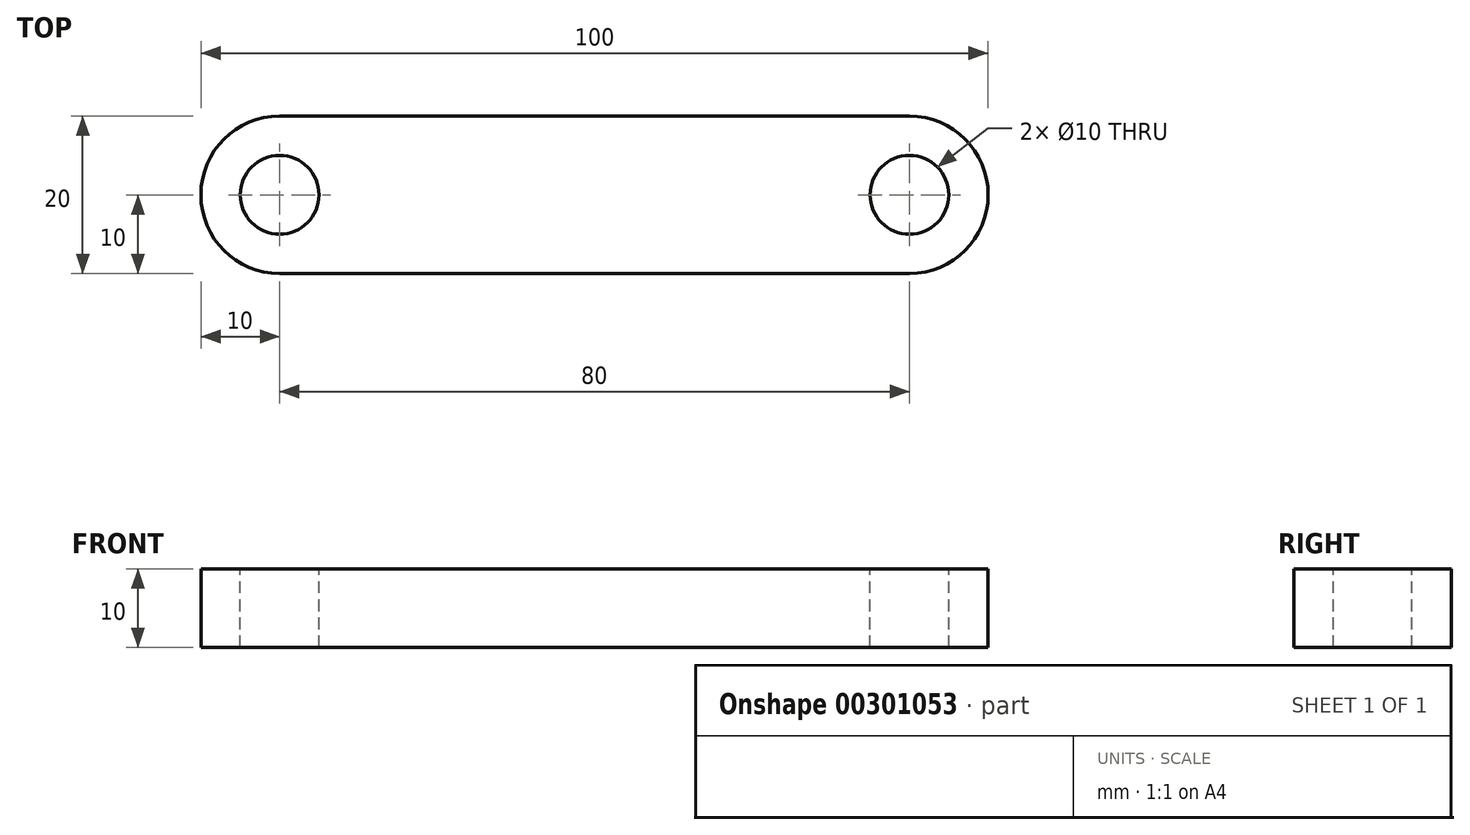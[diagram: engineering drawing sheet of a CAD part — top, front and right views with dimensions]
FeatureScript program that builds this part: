
annotation { "Feature Type Name" : "Feature", "Feature Type Description" : "" }
export const myFeature = defineFeature(function(context is Context, id is Id, definition is map)
    precondition{}
    {
        {
            var Q0;
            Q0=qCreatedBy(makeId("Top.planeOp"),FACE);
            var sketch = newSketch(context, id + "F0", { "sketchPlane" : qUnion([Q0])});
            skLineSegment(sketch, "E0", {"start": v(0, 0) * mm, "end": v(80, 0) * mm});
            skLineSegment(sketch, "E1", {"start": v(0, 20) * mm, "end": v(80, 20) * mm});
            skArc(sketch, "E2", {"start": v(0, 20) * mm, "mid": v(-10, 10) * mm, "end": v(0, 0) * mm});
            skArc(sketch, "E3", {"start": v(80, 0) * mm, "mid": v(90, 10) * mm, "end": v(80, 20) * mm});
            skSolve(sketch);
        }
        {
            var Q0;
            Q0=makeQuery(id+"F0.imprint","IMPRINT",FACE,{"disambiguationData":[TD([[makeQuery(id+"F0.imprint","IMPRINT",EDGE,{"derivedFrom":sQuery(id+"F0.wireOp",EDGE,"E0")}),1.0]])]});
            extrude(context, id + "F1", {"entities" : qUnion([Q0]), "depth" : 10 * mm});
        }
        {
            var Q0;
            Q0=makeQuery(id+"F1.opExtrude","CAP_FACE",FACE,{"disambiguationData":[OSD([sQuery(id+"F0.wireOp",EDGE,"E0"),sQuery(id+"F0.wireOp",EDGE,"E1"),sQuery(id+"F0.wireOp",EDGE,"E2"),sQuery(id+"F0.wireOp",EDGE,"E3")])],"isStart":false});
            var sketch = newSketch(context, id + "F2", { "sketchPlane" : qUnion([Q0])});
            skCircle(sketch, "E4", {"center": v(0, 10) * mm, "radius": 5 * mm});
            skCircle(sketch, "E5", {"center": v(80, 10) * mm, "radius": 5 * mm});
            skSolve(sketch);
        }
        {
            var Q0;
            Q0 = qSketchRegion(id + "F2", true);
            extrude(context, id + "F3", {"entities" : qUnion([Q0]), "operationType" : NewBodyOperationType.REMOVE, "endBound" : BoundingType.THROUGH_ALL, "oppositeDirection" : true, "depth" : 25 * mm});
        }
    });
